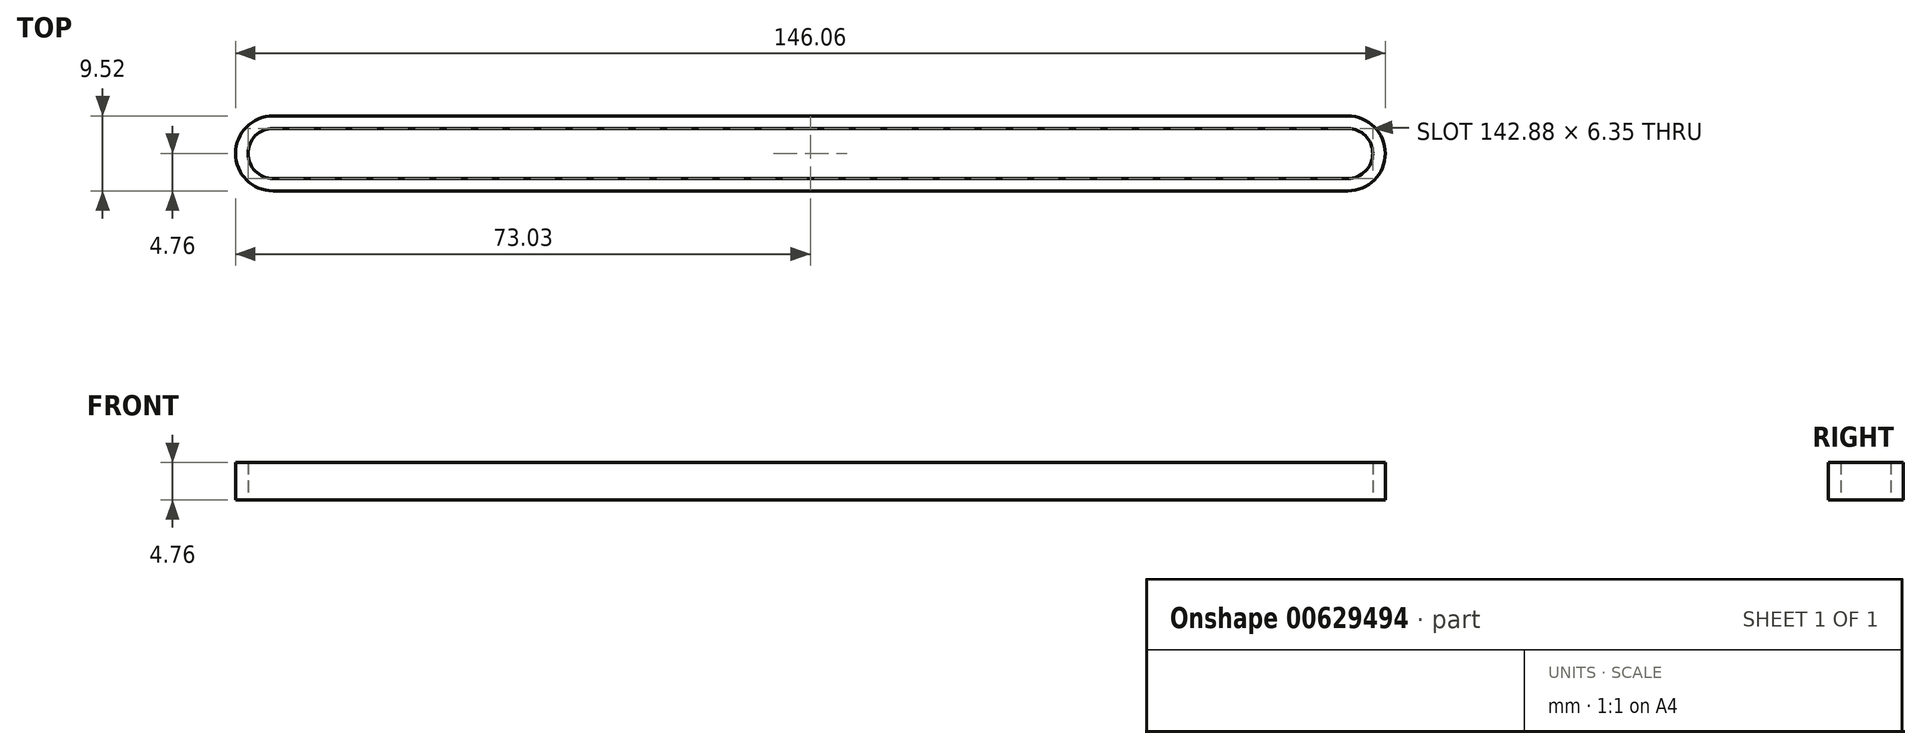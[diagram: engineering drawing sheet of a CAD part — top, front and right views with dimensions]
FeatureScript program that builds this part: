
annotation { "Feature Type Name" : "Feature", "Feature Type Description" : "" }
export const myFeature = defineFeature(function(context is Context, id is Id, definition is map)
    precondition{}
    {
        {
            var Q0;
            Q0=qCreatedBy(makeId("Top.planeOp"),FACE);
            var sketch = newSketch(context, id + "F0", { "sketchPlane" : qUnion([Q0])});
            skLineSegment(sketch, "E0.bottom", {"start": v(-68.26, 4.76) * mm, "end": v(68.26, 4.76) * mm});
            skLineSegment(sketch, "E0.top", {"start": v(-68.26, -4.76) * mm, "end": v(68.26, -4.76) * mm});
            skPoint(sketch, "E0.middle", {"position": v(0, 0) * mm});
            skArc(sketch, "E1", {"start": v(-68.26, 4.76) * mm, "mid": v(-73.03, 0) * mm, "end": v(-68.26, -4.76) * mm});
            skArc(sketch, "E2", {"start": v(68.26, -4.76) * mm, "mid": v(73.03, 0) * mm, "end": v(68.26, 4.76) * mm});
            skLineSegment(sketch, "E3.0", {"start": v(-68.26, -3.18) * mm, "end": v(68.26, -3.18) * mm});
            skArc(sketch, "E3.1", {"start": v(-68.26, 3.17) * mm, "mid": v(-71.44, 0) * mm, "end": v(-68.26, -3.18) * mm});
            skLineSegment(sketch, "E3.2", {"start": v(-68.26, 3.17) * mm, "end": v(68.26, 3.17) * mm});
            skArc(sketch, "E3.3", {"start": v(68.26, -3.18) * mm, "mid": v(71.44, 0) * mm, "end": v(68.26, 3.17) * mm});
            skSolve(sketch);
        }
        {
            var Q0;
            Q0=makeQuery(id+"F0.imprint","IMPRINT",FACE,{"disambiguationData":[TD([[makeQuery(id+"F0.imprint","IMPRINT",EDGE,{"derivedFrom":sQuery(id+"F0.wireOp",EDGE,"E0.bottom")}),-1.0]])]});
            extrude(context, id + "F1", {"entities" : qUnion([Q0]), "depth" : 4.76 * mm, "offsetDistance" : 25.4 * mm});
        }
    });
